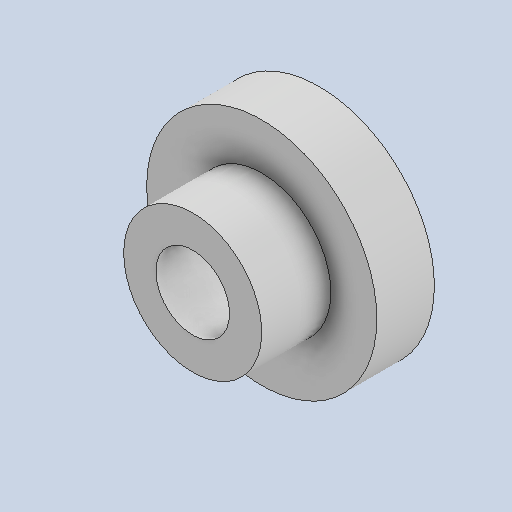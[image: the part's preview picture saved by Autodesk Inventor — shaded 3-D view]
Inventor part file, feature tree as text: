
AUTODESK INVENTOR PART (.ipt)
format: ipt  version: 2025.1 (Build 291241000, 241)  size: 124,928 bytes
history: native  units: mm
features: other x6, sketch x2, extrude x2, reference x1
ambient origin geometry x8: Origin, YZ Plane, XZ Plane, XY Plane, X Axis, Y Axis, Z Axis, Center Point
bodies: Body1 (feature_tree)
feature tree (11):
  other  "ソリッド1"
  sketch  "スケッチ1"
  other  "作業平面1"
  extrude  "押し出し1"  Depth=10.0mm
  sketch  "スケッチ2"
  other  "作業平面2"
  extrude  "押し出し2"  Depth=6.0mm
  reference  "参照1"
  other  "<userpath>\Documents\Inventor\Vixen\doutai.iam"
  other  "doutai.iam"
  other  "namida:1"
